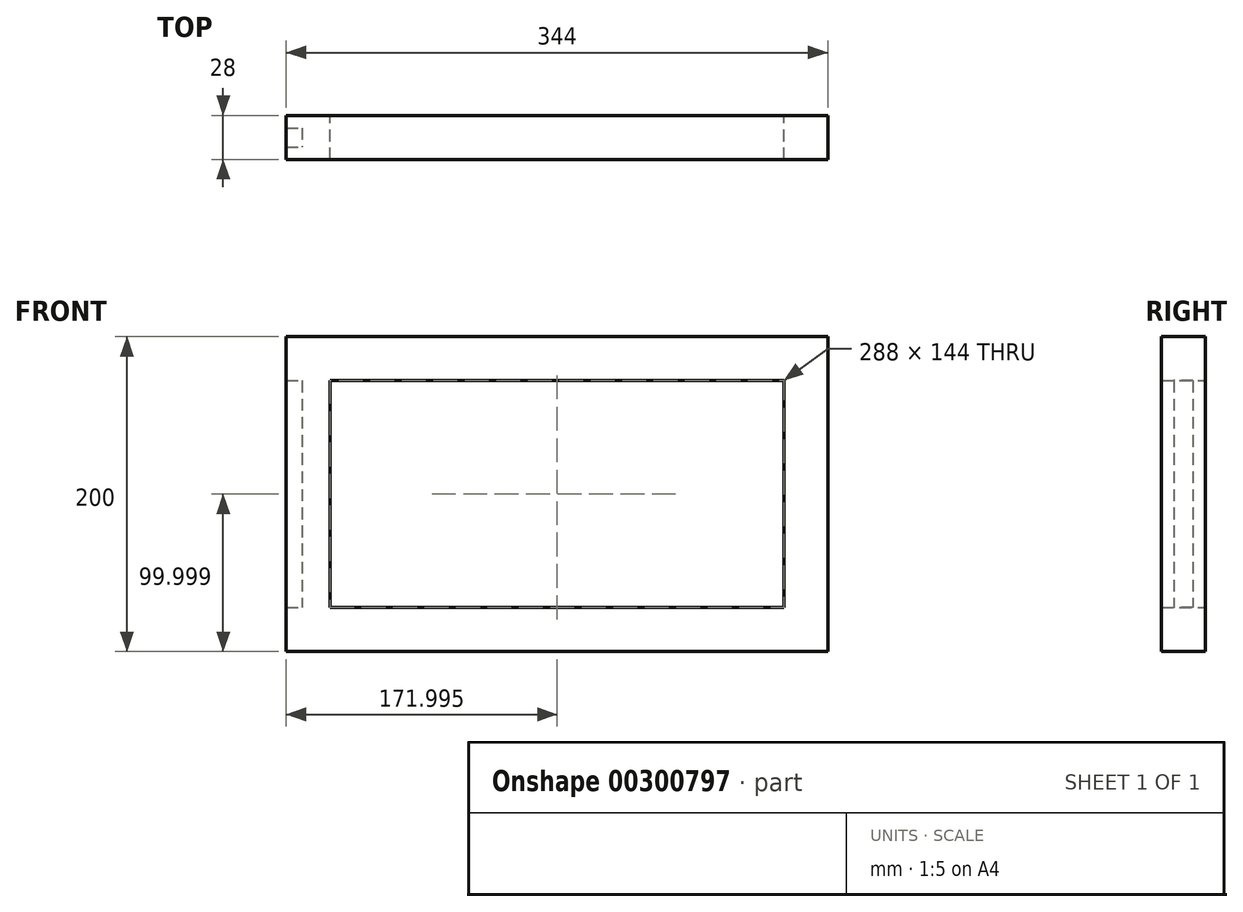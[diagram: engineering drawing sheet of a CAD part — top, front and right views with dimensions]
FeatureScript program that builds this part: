
annotation { "Feature Type Name" : "Feature", "Feature Type Description" : "" }
export const myFeature = defineFeature(function(context is Context, id is Id, definition is map)
    precondition{}
    {
        {
            var Q0;
            Q0=qCreatedBy(makeId("Front.planeOp"),FACE);
            var sketch = newSketch(context, id + "F0", { "sketchPlane" : qUnion([Q0])});
            skLineSegment(sketch, "E0.bottom", {"start": v(-491.01, 215.38) * mm, "end": v(368.99, 215.38) * mm});
            skLineSegment(sketch, "E0.top", {"start": v(-491.01, -284.62) * mm, "end": v(368.99, -284.62) * mm});
            skLineSegment(sketch, "E0.left", {"start": v(-491.01, 215.38) * mm, "end": v(-491.01, -284.62) * mm});
            skLineSegment(sketch, "E0.right", {"start": v(368.99, 215.38) * mm, "end": v(368.99, -284.62) * mm});
            skLineSegment(sketch, "E1.bottom", {"start": v(-421.01, 145.38) * mm, "end": v(298.99, 145.38) * mm});
            skLineSegment(sketch, "E1.top", {"start": v(-421.01, -214.62) * mm, "end": v(298.99, -214.62) * mm});
            skLineSegment(sketch, "E1.left", {"start": v(-421.01, 145.38) * mm, "end": v(-421.01, -214.62) * mm});
            skLineSegment(sketch, "E1.right", {"start": v(298.99, 145.38) * mm, "end": v(298.99, -214.62) * mm});
            skSolve(sketch);
        }
        {
            var Q0;
            Q0=makeQuery(id+"F0.imprint","IMPRINT",FACE,{"disambiguationData":[TD([[makeQuery(id+"F0.imprint","IMPRINT",EDGE,{"derivedFrom":sQuery(id+"F0.wireOp",EDGE,"E0.bottom")}),-1.0]])]});
            var Q1;
            Q1=qSketchRegion(id+"F2",true);
            extrude(context, id + "F1", {"entities" : qUnion([Q0, Q1]), "depth" : 70 * mm});
        }
        {
            var Q0;
            Q0=makeQuery(id+"F1.opExtrude","CAP_FACE",FACE,{"disambiguationData":[OSD([sQuery(id+"F0.wireOp",EDGE,"E0.bottom"),sQuery(id+"F0.wireOp",EDGE,"E0.top"),sQuery(id+"F0.wireOp",EDGE,"E0.left"),sQuery(id+"F0.wireOp",EDGE,"E0.right"),sQuery(id+"F0.wireOp",EDGE,"E1.bottom"),sQuery(id+"F0.wireOp",EDGE,"E1.top"),sQuery(id+"F0.wireOp",EDGE,"E1.left"),sQuery(id+"F0.wireOp",EDGE,"E1.right")])],"isStart":false});
            var sketch = newSketch(context, id + "F2", { "sketchPlane" : qUnion([Q0])});
            skSolve(sketch);
        }
        {
            var Q0;
            Q0=makeQuery(id+"F1.opExtrude","SWEPT_FACE",FACE,{"disambiguationData":[OSD([sQuery(id+"F0.wireOp",EDGE,"E0.left")])]});
            var sketch = newSketch(context, id + "F3", { "sketchPlane" : qUnion([Q0])});
            skLineSegment(sketch, "E2.bottom", {"start": v(20, 145.38) * mm, "end": v(50, 145.38) * mm});
            skLineSegment(sketch, "E2.top", {"start": v(20, -214.62) * mm, "end": v(50, -214.62) * mm});
            skLineSegment(sketch, "E2.left", {"start": v(20, 145.38) * mm, "end": v(20, -214.62) * mm});
            skLineSegment(sketch, "E2.right", {"start": v(50, 145.38) * mm, "end": v(50, -214.62) * mm});
            skSolve(sketch);
        }
        {
            var Q0;
            Q0=makeQuery(id+"F3.imprint","IMPRINT",FACE,{"disambiguationData":[TD([[makeQuery(id+"F3.imprint","IMPRINT",EDGE,{"derivedFrom":sQuery(id+"F3.wireOp",EDGE,"E2.bottom")}),-1.0]])]});
            extrude(context, id + "F4", {"entities" : qUnion([Q0]), "operationType" : NewBodyOperationType.REMOVE, "depth" : 25 * mm, "hasSecondDirection" : true, "secondDirectionOppositeDirection" : true, "secondDirectionDepth" : 25 * mm});
        }
        {
            var Q0;
            Q0=makeQuery(id+"F1.opExtrude","SWEPT_BODY",BODY,{"disambiguationData":[OSD([sQuery(id+"F0.wireOp",EDGE,"E0.bottom"),sQuery(id+"F0.wireOp",EDGE,"E0.top"),sQuery(id+"F0.wireOp",EDGE,"E0.left"),sQuery(id+"F0.wireOp",EDGE,"E0.right"),sQuery(id+"F0.wireOp",EDGE,"E1.bottom"),sQuery(id+"F0.wireOp",EDGE,"E1.top"),sQuery(id+"F0.wireOp",EDGE,"E1.left"),sQuery(id+"F0.wireOp",EDGE,"E1.right")])]});
            var Q1;
            Q1=makeQuery(id+"F1.opExtrude","CAP_VERTEX",VERTEX,{"disambiguationData":[OSD([sQuery(id+"F0.wireOp",EDGE,"E0.top"),sQuery(id+"F0.wireOp",EDGE,"E0.right")])],"isStart":false});
            var Q2;
            Q2=makeQuery(id+"F1.opExtrude","CAP_VERTEX",VERTEX,{"disambiguationData":[OSD([sQuery(id+"F0.wireOp",EDGE,"E0.top"),sQuery(id+"F0.wireOp",EDGE,"E0.left")])],"isStart":true});
            transform(context, id + "F5", {"entities" : qUnion([Q0]), "transformType" : TransformType.SCALE_UNIFORMLY, "scale" : 0.4, "scalePoint" : qUnion([Q2]), "makeCopy" : false});
        }
    });
